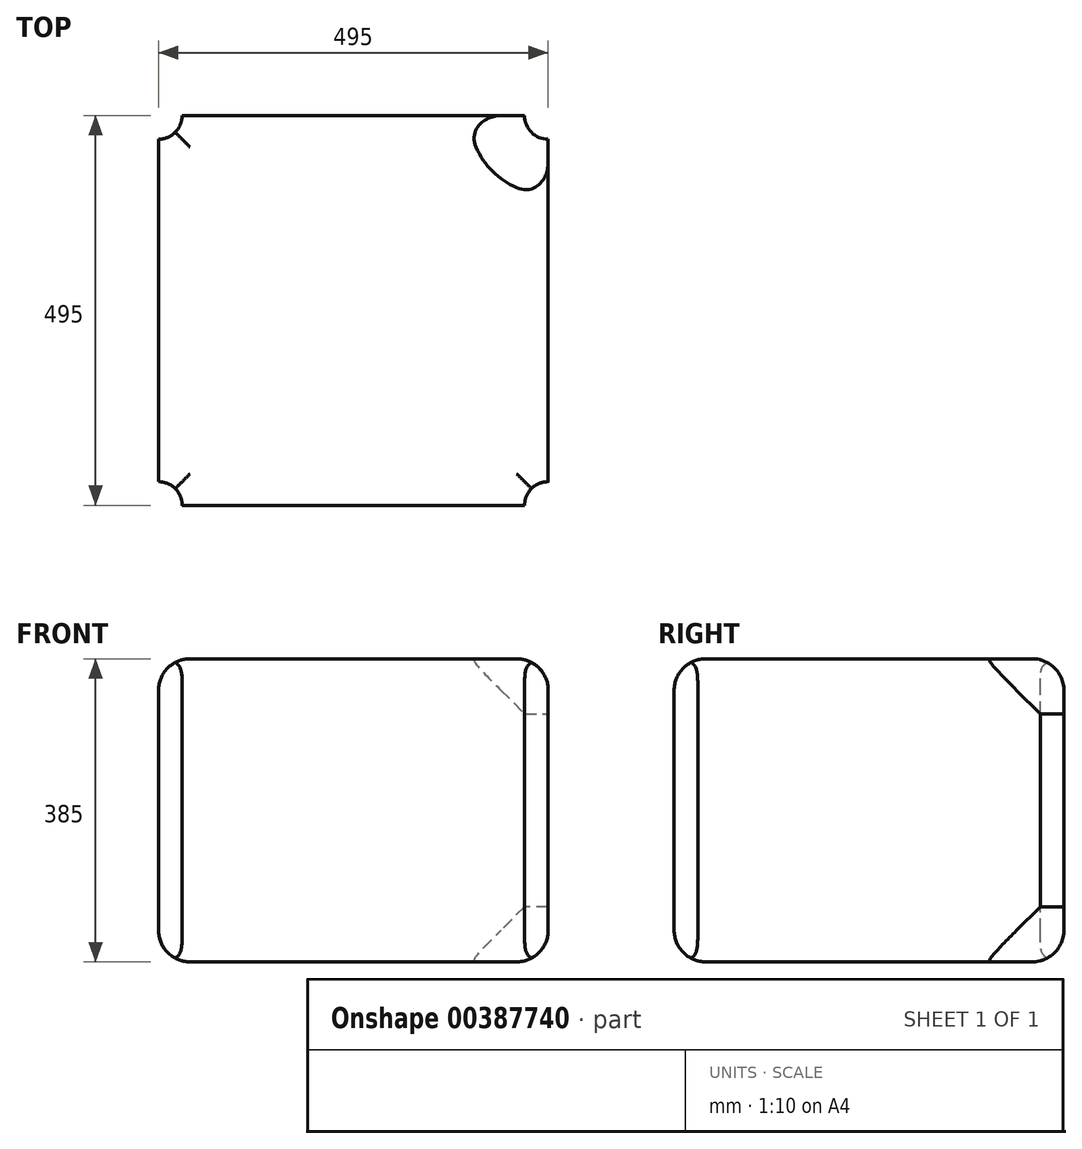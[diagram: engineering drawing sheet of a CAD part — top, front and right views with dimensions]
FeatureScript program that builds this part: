
annotation { "Feature Type Name" : "Feature", "Feature Type Description" : "" }
export const myFeature = defineFeature(function(context is Context, id is Id, definition is map)
    precondition{}
    {
        {
            var Q0;
            Q0=qCreatedBy(makeId("Top.planeOp"),FACE);
            var sketch = newSketch(context, id + "F0", { "sketchPlane" : qUnion([Q0])});
            skLineSegment(sketch, "E0.bottom", {"start": v(247.5, 247.5) * mm, "end": v(-247.5, 247.5) * mm});
            skLineSegment(sketch, "E0.top", {"start": v(247.5, -247.5) * mm, "end": v(-247.5, -247.5) * mm});
            skLineSegment(sketch, "E0.left", {"start": v(247.5, 247.5) * mm, "end": v(247.5, -247.5) * mm});
            skLineSegment(sketch, "E0.right", {"start": v(-247.5, 247.5) * mm, "end": v(-247.5, -247.5) * mm});
            skPoint(sketch, "E0.middle", {"position": v(0, 0) * mm});
            skSolve(sketch);
        }
        {
            var Q0;
            Q0=makeQuery(id+"F0.imprint","IMPRINT",FACE,{"disambiguationData":[TD([[makeQuery(id+"F0.imprint","IMPRINT",EDGE,{"derivedFrom":sQuery(id+"F0.wireOp",EDGE,"E0.bottom")}),1.0]])]});
            extrude(context, id + "F1", {"entities" : qUnion([Q0]), "depth" : 385 * mm});
        }
        {
            var Q0;
            Q0=makeQuery(id+"F1.opExtrude","CAP_EDGE",EDGE,{"disambiguationData":[OSD([sQuery(id+"F0.wireOp",EDGE,"E0.right")])],"isStart":false});
            var Q1;
            Q1=makeQuery(id+"F1.opExtrude","CAP_EDGE",EDGE,{"disambiguationData":[OSD([sQuery(id+"F0.wireOp",EDGE,"E0.top")])],"isStart":false});
            var Q2;
            Q2=makeQuery(id+"F1.opExtrude","CAP_EDGE",EDGE,{"disambiguationData":[OSD([sQuery(id+"F0.wireOp",EDGE,"E0.left")])],"isStart":false});
            var Q3;
            Q3=makeQuery(id+"F1.opExtrude","CAP_EDGE",EDGE,{"disambiguationData":[OSD([sQuery(id+"F0.wireOp",EDGE,"E0.bottom")])],"isStart":false});
            var Q4;
            Q4=makeQuery(id+"F1.opExtrude","CAP_EDGE",EDGE,{"disambiguationData":[OSD([sQuery(id+"F0.wireOp",EDGE,"E0.left")])],"isStart":true});
            var Q5;
            Q5=makeQuery(id+"F1.opExtrude","CAP_EDGE",EDGE,{"disambiguationData":[OSD([sQuery(id+"F0.wireOp",EDGE,"E0.top")])],"isStart":true});
            var Q6;
            Q6=makeQuery(id+"F1.opExtrude","CAP_EDGE",EDGE,{"disambiguationData":[OSD([sQuery(id+"F0.wireOp",EDGE,"E0.right")])],"isStart":true});
            var Q7;
            Q7=makeQuery(id+"F1.opExtrude","CAP_EDGE",EDGE,{"disambiguationData":[OSD([sQuery(id+"F0.wireOp",EDGE,"E0.bottom")])],"isStart":true});
            fillet(context, id + "F2", {"entities" : qUnion([Q0, Q1, Q2, Q3, Q4, Q5, Q6, Q7]), "radius" : 40 * mm, "tangentPropagation" : true, "allowEdgeOverflow" : false});
        }
        {
            var Q0;
            Q0=makeQuery(id+"F1.opExtrude","SWEPT_FACE",FACE,{"disambiguationData":[OSD([sQuery(id+"F0.wireOp",EDGE,"E0.left")])]});
            var sketch = newSketch(context, id + "F3", { "sketchPlane" : qUnion([Q0])});
            skPoint(sketch, "E1", {"position": v(247.5, 285) * mm});
            skLineSegment(sketch, "E2", {"start": v(247.5, 285) * mm, "end": v(147.5, 385) * mm});
            skLineSegment(sketch, "E3", {"start": v(247.5, 385) * mm, "end": v(247.5, 285) * mm});
            skLineSegment(sketch, "E4", {"start": v(247.5, 385) * mm, "end": v(147.5, 385) * mm});
            skLineSegment(sketch, "E5", {"start": v(247.5, 52.94) * mm, "end": v(247.5, 538.16) * mm});
            skLineSegment(sketch, "E6", {"start": v(247.5, 100) * mm, "end": v(147.5, 0) * mm});
            skLineSegment(sketch, "E7", {"start": v(147.5, 0) * mm, "end": v(247.5, 0) * mm});
            skLineSegment(sketch, "E8", {"start": v(247.5, 0) * mm, "end": v(247.5, 100) * mm});
            skSolve(sketch);
        }
        {
            var Q0;
            Q0 = qSketchRegion(id + "F3", true);
            var Q1;
            Q1=sQuery(id+"F3.wireOp",EDGE,"E5");
            revolve(context, id + "F4", {"operationType" : NewBodyOperationType.REMOVE, "entities" : qUnion([Q0]), "axis" : qUnion([Q1]), "revolveType" : RevolveType.FULL, "oppositeDirection" : true});
        }
        {
            var Q0;
            Q0=makeQuery(id+"F1.opExtrude","CAP_FACE",FACE,{"disambiguationData":[OSD([sQuery(id+"F0.wireOp",EDGE,"E0.bottom"),sQuery(id+"F0.wireOp",EDGE,"E0.top"),sQuery(id+"F0.wireOp",EDGE,"E0.left"),sQuery(id+"F0.wireOp",EDGE,"E0.right")])],"isStart":false});
            var sketch = newSketch(context, id + "F5", { "sketchPlane" : qUnion([Q0])});
            skPoint(sketch, "E9", {"position": v(247.5, 247.5) * mm});
            skPoint(sketch, "E10", {"position": v(-247.5, 247.5) * mm});
            skPoint(sketch, "E11", {"position": v(-247.5, -247.5) * mm});
            skPoint(sketch, "E12", {"position": v(247.5, -247.5) * mm});
            skCircle(sketch, "E13", {"center": v(247.5, 247.5) * mm, "radius": 30 * mm});
            skCircle(sketch, "E14", {"center": v(-247.5, 247.5) * mm, "radius": 30 * mm});
            skCircle(sketch, "E15", {"center": v(-247.5, -247.5) * mm, "radius": 30 * mm});
            skCircle(sketch, "E16", {"center": v(247.5, -247.5) * mm, "radius": 30 * mm});
            skSolve(sketch);
        }
        {
            var Q0;
            Q0 = qSketchRegion(id + "F5", true);
            var Q1;
            Q1=makeQuery(id+"F1.opExtrude","CAP_FACE",FACE,{"disambiguationData":[OSD([sQuery(id+"F0.wireOp",EDGE,"E0.bottom"),sQuery(id+"F0.wireOp",EDGE,"E0.top"),sQuery(id+"F0.wireOp",EDGE,"E0.left"),sQuery(id+"F0.wireOp",EDGE,"E0.right")])],"isStart":true});
            var Q2;
            Q2=makeQuery(id+"F1.opExtrude","CAP_FACE",FACE,{"disambiguationData":[OSD([sQuery(id+"F0.wireOp",EDGE,"E0.bottom"),sQuery(id+"F0.wireOp",EDGE,"E0.top"),sQuery(id+"F0.wireOp",EDGE,"E0.left"),sQuery(id+"F0.wireOp",EDGE,"E0.right")])],"isStart":true});
            extrude(context, id + "F6", {"entities" : qUnion([Q0, Q1]), "operationType" : NewBodyOperationType.REMOVE, "endBound" : BoundingType.THROUGH_ALL, "oppositeDirection" : true, "endBoundEntityFace" : qUnion([Q2]), "depth" : 25 * mm});
        }
    });
